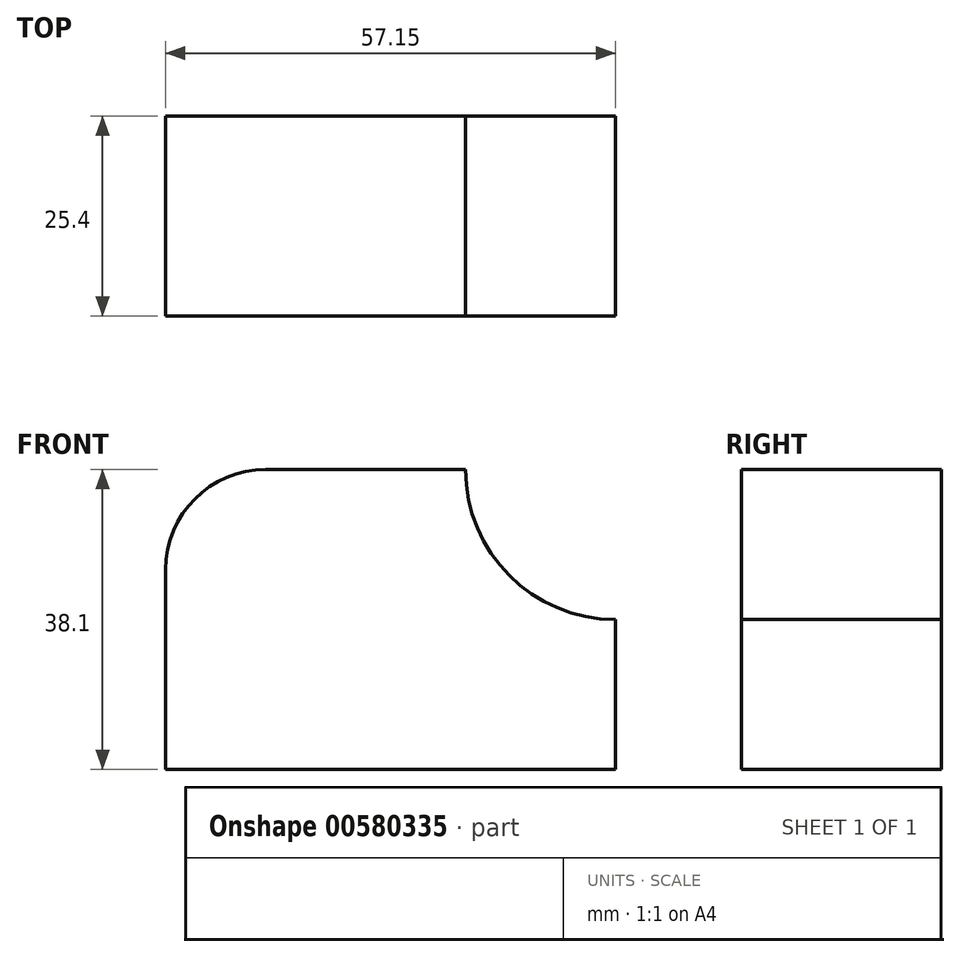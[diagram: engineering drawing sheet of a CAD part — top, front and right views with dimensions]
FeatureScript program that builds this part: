
annotation { "Feature Type Name" : "Feature", "Feature Type Description" : "" }
export const myFeature = defineFeature(function(context is Context, id is Id, definition is map)
    precondition{}
    {
        {
            var Q0;
            Q0=qCreatedBy(makeId("Front.planeOp"),FACE);
            var sketch = newSketch(context, id + "F0", { "sketchPlane" : qUnion([Q0])});
            skLineSegment(sketch, "E0", {"start": v(0, 0) * mm, "end": v(57.15, 0) * mm});
            skLineSegment(sketch, "E1", {"start": v(57.15, 0) * mm, "end": v(57.15, 38.1) * mm});
            skLineSegment(sketch, "E2", {"start": v(57.15, 38.1) * mm, "end": v(0, 38.1) * mm});
            skLineSegment(sketch, "E3", {"start": v(0, 38.1) * mm, "end": v(0, 0) * mm});
            skSolve(sketch);
        }
        {
            var Q0;
            Q0=makeQuery(id+"F0.imprint","IMPRINT",FACE,{"disambiguationData":[TD([[makeQuery(id+"F0.imprint","IMPRINT",EDGE,{"derivedFrom":sQuery(id+"F0.wireOp",EDGE,"E0")}),1.0]])]});
            extrude(context, id + "F1", {"entities" : qUnion([Q0]), "depth" : 25.4 * mm, "offsetDistance" : 25.4 * mm});
        }
        {
            var Q0;
            Q0=makeQuery(id+"F1.opExtrude","CAP_FACE",FACE,{"disambiguationData":[OSD([sQuery(id+"F0.wireOp",EDGE,"E0"),sQuery(id+"F0.wireOp",EDGE,"E1"),sQuery(id+"F0.wireOp",EDGE,"E2"),sQuery(id+"F0.wireOp",EDGE,"E3")])],"isStart":false});
            var sketch = newSketch(context, id + "F2", { "sketchPlane" : qUnion([Q0])});
            skArc(sketch, "E4", {"start": v(38.1, 38.1) * mm, "mid": v(43.68, 24.63) * mm, "end": v(57.15, 19.05) * mm});
            skArc(sketch, "E5", {"start": v(12.7, 38.1) * mm, "mid": v(3.72, 34.38) * mm, "end": v(0, 25.4) * mm});
            skSolve(sketch);
        }
        {
            var Q0;
            {var subQ0=sQuery(id+"F2.wireOp",EDGE,"E5");Q0=makeQuery(id+"F2.imprint","IMPRINT",FACE,{"disambiguationData":[TD([[makeQuery(id+"F2.imprint","IMPRINT",EDGE,{"derivedFrom":subQ0}),-1.0]])]});}
            var Q1;
            {var subQ0=sQuery(id+"F2.wireOp",EDGE,"E4");Q1=makeQuery(id+"F2.imprint","IMPRINT",FACE,{"disambiguationData":[TD([[makeQuery(id+"F2.imprint","IMPRINT",EDGE,{"derivedFrom":subQ0}),1.0]])]});}
            extrude(context, id + "F3", {"entities" : qUnion([Q0, Q1]), "operationType" : NewBodyOperationType.REMOVE, "oppositeDirection" : true, "depth" : 25.4 * mm, "offsetDistance" : 25.4 * mm});
        }
    });
